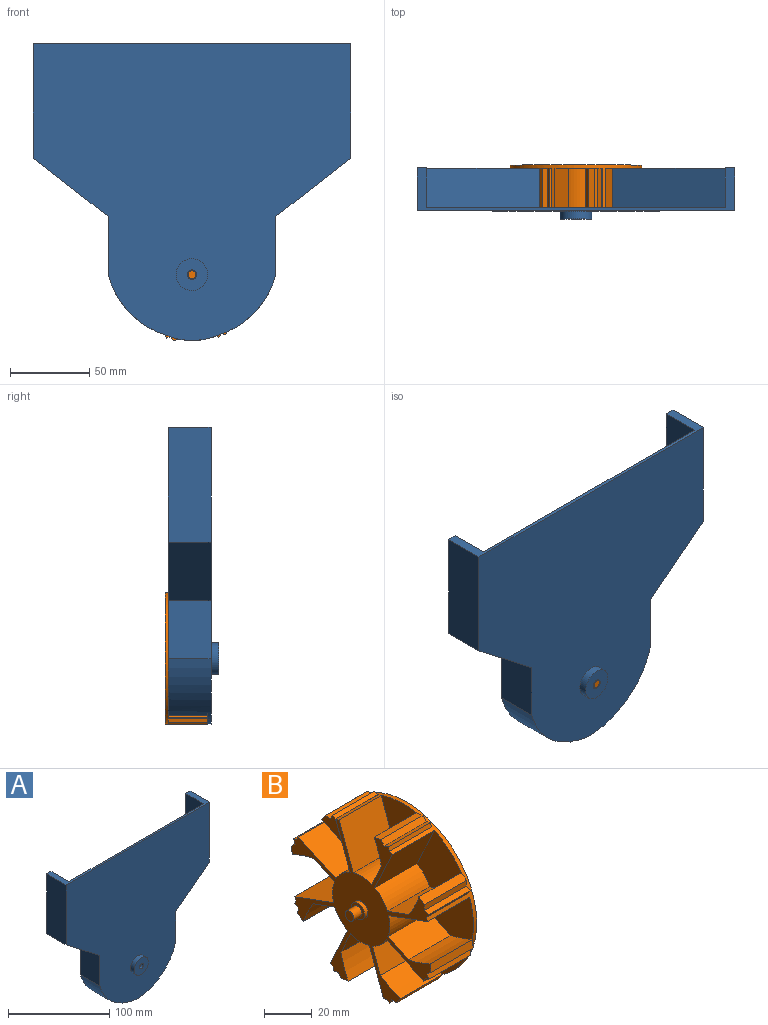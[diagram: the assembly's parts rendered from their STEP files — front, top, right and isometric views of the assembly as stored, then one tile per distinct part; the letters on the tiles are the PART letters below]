
ASSEMBLY  parts=2 mates=1
PART A: 27 faces, bbox 200x32x187.1 mm
  f0: plane 188x187.15mm, normal (0,1,0), area 23352mm2, adj f1,f2,f6,f10,f14,f17,f18,f19
  f1: cylinder r=41.5mm len=31.76mm, axis (0,1,0), area 65.2mm2, adj f0,f2,f10,f11
  f2: cylinder r=54.6mm len=38.34mm, axis (0,1,0), area 1322.3mm2, adj f0,f1,f3,f11,f24,f25
  f3: plane 36.63x27mm, normal (1,0,0), area 989mm2, adj f2,f4,f11,f24
  f4: plane 47.2x36.66mm, normal (0.61,0,-0.79), area 1613.6mm2, adj f3,f5,f11,f24
  f5: plane 72.36x27mm, normal (1,0,0), area 1953.7mm2, adj f4,f6,f11,f24
  f6: plane 200x27mm, normal (0,0,1), area 700mm2, adj f0,f5,f7,f11,f19,f20,f21,f24
  f7: plane 72.36x27mm, normal (-1,0,0), area 1953.7mm2, adj f6,f8,f11,f20
  f8: plane 47.2x36.66mm, normal (-0.61,0,-0.79), area 1613.6mm2, adj f7,f9,f11,f20
  f9: plane 36.63x27mm, normal (-1,0,0), area 989mm2, adj f8,f10,f11,f20
  f10: cylinder r=54.6mm len=38.34mm, axis (0,1,0), area 1322.3mm2, adj f0,f1,f9,f11,f20,f26
  f11: plane 200x187.15mm, normal (0,-1,0), area 26826.5mm2, adj f1,f2,f3,f4,f5,f6,f7,f8
  f12: cylinder r=10mm len=20mm, axis (0,1,0), area 314.2mm2, adj f11,f13
  f13: plane 20x20mm, normal (0,-1,0), area 285.9mm2, adj f12,f16
  f14: cylinder r=8mm len=16mm, axis (0,1,0), area 201.1mm2, adj f0,f15
  f15: plane 16x16mm, normal (0,1,0), area 172.8mm2, adj f14,f16
  f16: cylinder r=3mm len=6mm, axis (0,1,0), area 56.5mm2, adj f13,f15
  f17: cylinder r=44.81mm len=37.39mm, axis (0,-1,0), area 1126.7mm2, adj f0,f18,f20,f26
  f18: plane 70.83x35.9mm, normal (0.45,0,0.89), area 1985.2mm2, adj f0,f17,f19,f20
  f19: plane 72.36x25mm, normal (1,0,0), area 1809mm2, adj f0,f6,f18,f20
  f20: plane 181.46x77.43mm, normal (0,1,0), area 1793.8mm2, adj f6,f7,f8,f9,f10,f17,f18,f19
  f21: plane 72.36x25mm, normal (-1,0,0), area 1809mm2, adj f0,f6,f22,f24
  f22: plane 70.83x35.9mm, normal (-0.45,0,0.89), area 1985.2mm2, adj f0,f21,f23,f24
  f23: cylinder r=44.81mm len=37.39mm, axis (0,-1,0), area 1126.7mm2, adj f0,f22,f24,f25
  f24: plane 181.46x77.43mm, normal (0,1,0), area 1793.8mm2, adj f2,f3,f4,f5,f6,f21,f22,f23
  f25: cylinder r=44.9mm len=35.82mm, axis (0,-1,0), area 1097mm2, adj f0,f2,f23,f24
  f26: cylinder r=44.9mm len=35.82mm, axis (0,-1,0), area 1097mm2, adj f0,f10,f17,f20
PART B: 97 faces, bbox 34x83x83 mm
  f0: plane 25x12.24mm, normal (0,0.42,-0.91), area 337.7mm2, adj f12,f13,f32,f84
  f1: plane 25x12.69mm, normal (0,-0.34,-0.94), area 337.7mm2, adj f11,f13,f33,f77
  f2: plane 25x12.24mm, normal (0,-0.91,-0.42), area 337.7mm2, adj f8,f13,f34,f70
  f3: plane 25x12.69mm, normal (0,-0.94,0.34), area 337.7mm2, adj f7,f13,f35,f63
  f4: plane 25x12.69mm, normal (0,0.34,0.94), area 337.7mm2, adj f6,f13,f37,f49
  f5: plane 25.72x25.08mm, normal (-1,0,0), area 461.7mm2, adj f15,f16,f17,f38,f45
  f6: plane 30.44x26.17mm, normal (-1,0,0), area 465mm2, adj f4,f15,f18,f37,f49
  f7: plane 30.44x26.17mm, normal (-1,0,0), area 465mm2, adj f3,f15,f21,f35,f63
  f8: plane 25.72x25.21mm, normal (-1,0,0), area 465mm2, adj f2,f15,f22,f34,f70
  f9: plane 25.72x25.21mm, normal (-1,0,0), area 465mm2, adj f15,f19,f20,f36,f56
  f10: plane 30.63x30.57mm, normal (-1,0,0), area 468.4mm2, adj f15,f25,f26,f31,f90,f95
  f11: plane 30.44x26.17mm, normal (-1,0,0), area 465mm2, adj f1,f15,f23,f33,f77
  f12: plane 25.72x25.21mm, normal (-1,0,0), area 465mm2, adj f0,f15,f24,f32,f84
  f13: plane 82.83x82.83mm, normal (-1,0,0), area 1641.3mm2, adj f0,f1,f2,f3,f4,f15,f16,f17
  f14: plane 83x83mm, normal (1,0,0), area 5410.6mm2, adj f15
  f15: cylinder r=41.5mm len=83mm, axis (-1,0,0), area 921.5mm2, adj f5,f6,f7,f8,f9,f10,f11,f12
  f16: plane 25x23.07mm, normal (0,-0.94,0.34), area 613.7mm2, adj f5,f13,f15,f38
  f17: plane 25x12.24mm, normal (0,0.91,0.42), area 337.7mm2, adj f5,f13,f38,f45
  f18: plane 25x22.24mm, normal (0,-0.91,-0.42), area 613.6mm2, adj f6,f13,f15,f37
  f19: plane 25x23.06mm, normal (0,-0.34,-0.94), area 613.6mm2, adj f9,f13,f15,f36
  f20: plane 25x12.24mm, normal (0,-0.42,0.91), area 337.7mm2, adj f9,f13,f36,f56
  f21: plane 25x22.24mm, normal (0,0.42,-0.91), area 613.6mm2, adj f7,f13,f15,f35
  f22: plane 25x23.06mm, normal (0,0.94,-0.34), area 613.6mm2, adj f8,f13,f15,f34
  f23: plane 25x22.24mm, normal (0,0.91,0.42), area 613.6mm2, adj f11,f13,f15,f33
  f24: plane 25x23.06mm, normal (0,0.34,0.94), area 613.6mm2, adj f12,f13,f15,f32
  f25: plane 25x22.24mm, normal (0,-0.42,0.91), area 613.6mm2, adj f10,f13,f15,f31
  f26: plane 25x23.06mm, normal (0,0.94,-0.34), area 613.5mm2, adj f10,f13,f15,f31
  f27: cylinder r=4mm len=8mm, axis (1,0,0), area 50.3mm2, adj f13,f28
  f28: plane 8x8mm, normal (-1,0,0), area 30.6mm2, adj f27,f29
  f29: cylinder r=2.5mm len=5mm, axis (1,0,0), area 78.5mm2, adj f28,f30
  f30: plane 5x5mm, normal (-1,0,0), area 19.6mm2, adj f29
  f31: cylinder r=16.97mm len=25mm, axis (1,0,0), area 286.7mm2, adj f10,f13,f25,f26
  f32: cylinder r=16.97mm len=25mm, axis (1,0,0), area 283.2mm2, adj f0,f12,f13,f24
  f33: cylinder r=16.97mm len=25mm, axis (1,0,0), area 283.2mm2, adj f1,f11,f13,f23
  f34: cylinder r=16.97mm len=25mm, axis (1,0,0), area 283.2mm2, adj f2,f8,f13,f22
  f35: cylinder r=16.97mm len=25mm, axis (1,0,0), area 283.2mm2, adj f3,f7,f13,f21
  f36: cylinder r=16.97mm len=25mm, axis (1,0,0), area 283.2mm2, adj f9,f13,f19,f20
  f37: cylinder r=16.97mm len=25mm, axis (1,0,0), area 283.2mm2, adj f4,f6,f13,f18
  f38: cylinder r=16.97mm len=25mm, axis (1,0,0), area 279.8mm2, adj f5,f13,f16,f17
  f39: plane 6.02x2.22mm, normal (1,0,0), area 4.6mm2, adj f15,f43,f44
  f40: plane 2.99x2mm, normal (1,0,0), area 2.6mm2, adj f15,f41,f42
  f41: plane 25x2mm, normal (0,-0.97,0.26), area 51.9mm2, adj f13,f15,f40,f42
  f42: plane 25x2.44mm, normal (0,0.32,0.95), area 64.5mm2, adj f13,f40,f41,f43
  f43: plane 25x2.22mm, normal (0,-0.74,0.67), area 74.7mm2, adj f13,f39,f42,f44
  f44: plane 25x4.02mm, normal (0,0.15,0.99), area 101.6mm2, adj f13,f39,f43,f45
  f45: cylinder r=50.07mm len=25mm, axis (-1,0,0), area 338.3mm2, adj f5,f13,f17,f44
  f46: plane 5.39x3.28mm, normal (1,0,0), area 4.6mm2, adj f15,f48,f52
  f47: plane 2.94x2.32mm, normal (1,0,0), area 2.6mm2, adj f15,f50,f51
  f48: plane 25x3.28mm, normal (0,-0.59,0.81), area 101.6mm2, adj f13,f46,f49,f52
  f49: cylinder r=50.07mm len=25mm, axis (-1,0,0), area 338.3mm2, adj f4,f6,f13,f48
  f50: plane 25x1.8mm, normal (0,-0.87,-0.5), area 51.9mm2, adj f13,f15,f47,f51
  f51: plane 25x2.32mm, normal (0,-0.44,0.9), area 64.5mm2, adj f13,f47,f50,f52
  f52: plane 25x2.99mm, normal (0,-1,-0.05), area 74.7mm2, adj f13,f46,f48,f51
  f53: plane 6.02x2.22mm, normal (1,0,0), area 4.6mm2, adj f15,f55,f59
  f54: plane 2.99x2mm, normal (1,0,0), area 2.6mm2, adj f15,f57,f58
  f55: plane 25x4.02mm, normal (0,-0.99,0.15), area 101.6mm2, adj f13,f53,f56,f59
  f56: cylinder r=50.07mm len=25mm, axis (-1,0,0), area 338.3mm2, adj f9,f13,f20,f55
  f57: plane 25x2mm, normal (0,-0.26,-0.97), area 51.9mm2, adj f13,f15,f54,f58
  f58: plane 25x2.44mm, normal (0,-0.95,0.32), area 64.5mm2, adj f13,f54,f57,f59
  f59: plane 25x2.22mm, normal (0,-0.67,-0.74), area 74.7mm2, adj f13,f53,f55,f58
  f60: plane 5.39x3.28mm, normal (1,0,0), area 4.6mm2, adj f15,f62,f66
  f61: plane 2.94x2.32mm, normal (1,0,0), area 2.6mm2, adj f15,f64,f65
  f62: plane 25x3.28mm, normal (0,-0.81,-0.59), area 101.6mm2, adj f13,f60,f63,f66
  f63: cylinder r=50.07mm len=25mm, axis (-1,0,0), area 338.3mm2, adj f3,f7,f13,f62
  f64: plane 25x1.8mm, normal (0,0.5,-0.87), area 51.9mm2, adj f13,f15,f61,f65
  f65: plane 25x2.32mm, normal (0,-0.9,-0.44), area 64.5mm2, adj f13,f61,f64,f66
  f66: plane 25x2.99mm, normal (0,0.05,-1), area 74.7mm2, adj f13,f60,f62,f65
  f67: plane 6.02x2.22mm, normal (1,0,0), area 4.6mm2, adj f15,f69,f73
  f68: plane 2.99x2mm, normal (1,0,0), area 2.6mm2, adj f15,f71,f72
  f69: plane 25x4.02mm, normal (0,-0.15,-0.99), area 101.6mm2, adj f13,f67,f70,f73
  f70: cylinder r=50.07mm len=25mm, axis (-1,0,0), area 338.3mm2, adj f2,f8,f13,f69
  f71: plane 25x2mm, normal (0,0.97,-0.26), area 51.9mm2, adj f13,f15,f68,f72
  f72: plane 25x2.44mm, normal (0,-0.32,-0.95), area 64.5mm2, adj f13,f68,f71,f73
  f73: plane 25x2.22mm, normal (0,0.74,-0.67), area 74.7mm2, adj f13,f67,f69,f72
  f74: plane 5.39x3.28mm, normal (1,0,0), area 4.6mm2, adj f15,f76,f80
  f75: plane 2.94x2.32mm, normal (1,0,0), area 2.6mm2, adj f15,f78,f79
  f76: plane 25x3.28mm, normal (0,0.59,-0.81), area 101.6mm2, adj f13,f74,f77,f80
  f77: cylinder r=50.07mm len=25mm, axis (-1,0,0), area 338.3mm2, adj f1,f11,f13,f76
  f78: plane 25x1.8mm, normal (0,0.87,0.5), area 51.9mm2, adj f13,f15,f75,f79
  f79: plane 25x2.32mm, normal (0,0.44,-0.9), area 64.5mm2, adj f13,f75,f78,f80
  f80: plane 25x2.99mm, normal (0,1,0.05), area 74.7mm2, adj f13,f74,f76,f79
  f81: plane 6.02x2.22mm, normal (1,0,0), area 4.6mm2, adj f15,f83,f87
  f82: plane 2.99x2mm, normal (1,0,0), area 2.6mm2, adj f15,f85,f86
  f83: plane 25x4.02mm, normal (0,0.99,-0.15), area 101.6mm2, adj f13,f81,f84,f87
  f84: cylinder r=50.07mm len=25mm, axis (-1,0,0), area 338.3mm2, adj f0,f12,f13,f83
  f85: plane 25x2mm, normal (0,0.26,0.97), area 51.9mm2, adj f13,f15,f82,f86
  f86: plane 25x2.44mm, normal (0,0.95,-0.32), area 64.5mm2, adj f13,f82,f85,f87
  f87: plane 25x2.22mm, normal (0,0.67,0.74), area 74.7mm2, adj f13,f81,f83,f86
  f88: plane 5.39x3.28mm, normal (1,0,0), area 4.6mm2, adj f15,f93,f94
  f89: plane 2.94x2.32mm, normal (1,0,0), area 2.6mm2, adj f15,f91,f92
  f90: plane 25x10.37mm, normal (0,-0.94,0.34), area 275.9mm2, adj f10,f91,f95,f96
  f91: plane 25x1.8mm, normal (0,-0.5,0.87), area 51.9mm2, adj f89,f90,f92,f96
  f92: plane 25x2.32mm, normal (0,0.9,0.44), area 64.5mm2, adj f89,f91,f93,f96
  f93: plane 25x2.99mm, normal (0,-0.05,1), area 74.7mm2, adj f88,f92,f94,f96
  f94: plane 25x3.28mm, normal (0,0.81,0.59), area 101.6mm2, adj f88,f93,f95,f96
  f95: cylinder r=50.07mm len=25mm, axis (-1,0,0), area 338.3mm2, adj f10,f90,f94,f96
  f96: plane 12.1x11.4mm, normal (-1,0,0), area 56.3mm2, adj f90,f91,f92,f93,f94,f95
PLACE A t=(-64.1,31.19,-2.77)mm
PLACE B rot(axis=(-0.58,-0.58,0.58),120deg) t=(-64.1,31.19,-2.77)mm
MATE revolute B.f15 <-> A.f1  axis (0,-1,0) through (-64.1,24.19,-2.77)mm
